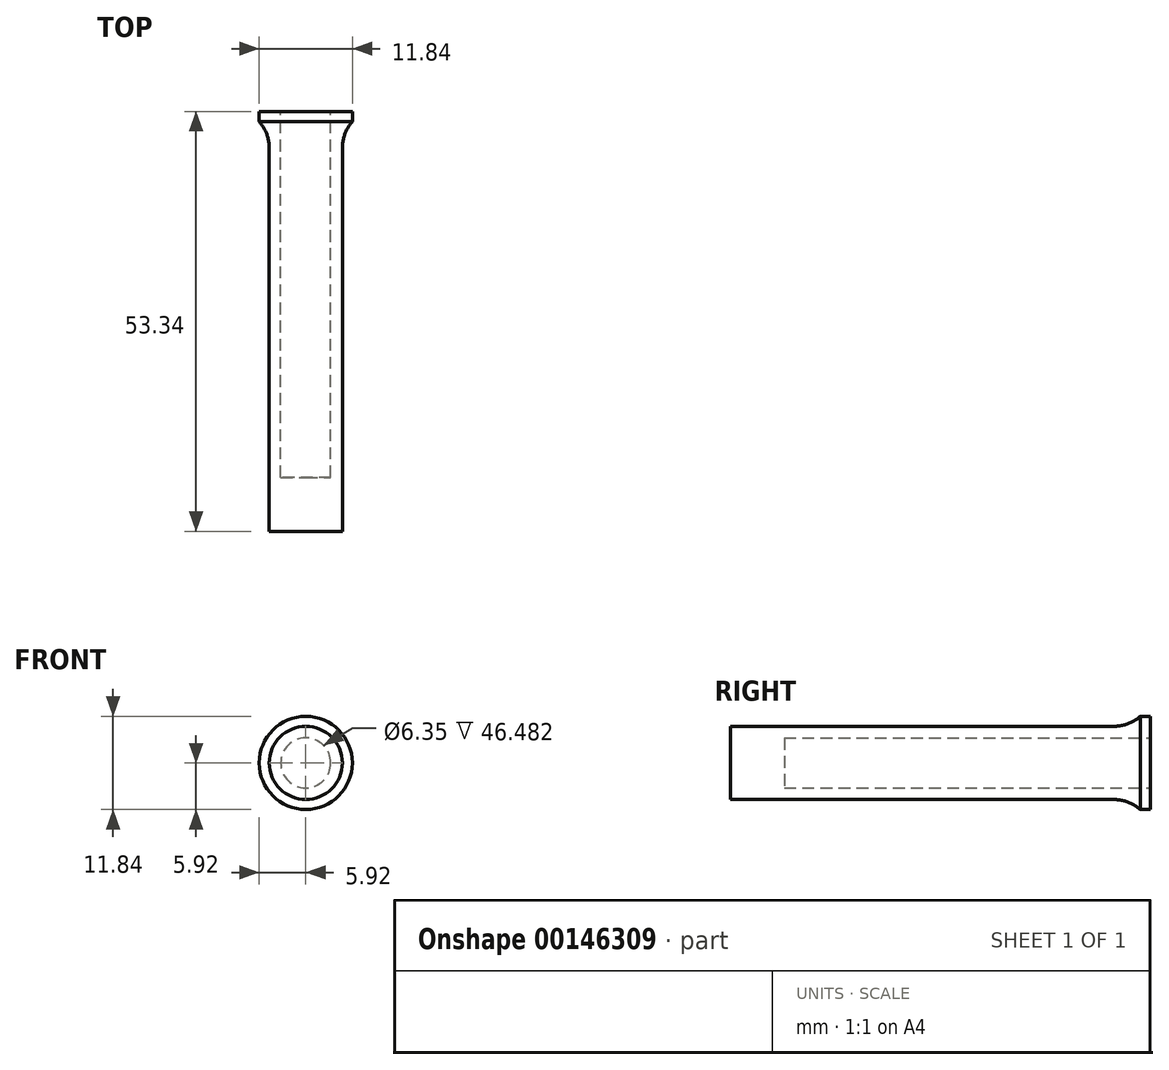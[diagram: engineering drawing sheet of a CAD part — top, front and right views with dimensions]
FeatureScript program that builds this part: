
annotation { "Feature Type Name" : "Feature", "Feature Type Description" : "" }
export const myFeature = defineFeature(function(context is Context, id is Id, definition is map)
    precondition{}
    {
        {
            var Q0;
            Q0=qCreatedBy(makeId("Top.planeOp"),FACE);
            var sketch = newSketch(context, id + "F0", { "sketchPlane" : qUnion([Q0])});
            skLineSegment(sketch, "E0", {"start": v(0, 0) * mm, "end": v(-4.65, 0) * mm});
            skLineSegment(sketch, "E1", {"start": v(-4.65, 0) * mm, "end": v(-4.65, 52.07) * mm});
            skLineSegment(sketch, "E2", {"start": v(-4.65, 53.34) * mm, "end": v(-3.18, 53.34) * mm});
            skLineSegment(sketch, "E3", {"start": v(-3.18, 53.34) * mm, "end": v(-3.17, 6.86) * mm});
            skLineSegment(sketch, "E4", {"start": v(-3.18, 6.86) * mm, "end": v(0, 6.86) * mm});
            skLineSegment(sketch, "E5", {"start": v(0, 6.86) * mm, "end": v(0, 0) * mm});
            skLineSegment(sketch, "E6", {"start": v(-4.65, 53.34) * mm, "end": v(-5.92, 53.34) * mm});
            skLineSegment(sketch, "E7", {"start": v(-5.92, 53.34) * mm, "end": v(-5.92, 52.07) * mm});
            skLineSegment(sketch, "E8", {"start": v(-5.92, 52.07) * mm, "end": v(-4.65, 52.07) * mm});
            skSolve(sketch);
        }
        {
            var Q0;
            Q0 = qSketchRegion(id + "F0", true);
            var Q1;
            Q1=sQuery(id+"F0.wireOp",EDGE,"E5");
            revolve(context, id + "F1", {"entities" : qUnion([Q0]), "axis" : qUnion([Q1]), "revolveType" : RevolveType.FULL});
        }
        {
            var Q0;
            Q0=makeQuery(id+"F1.opRevolve","SWEPT_EDGE",EDGE,{"disambiguationData":[OSD([sQuery(id+"F0.wireOp",EDGE,"E1"),sQuery(id+"F0.wireOp",EDGE,"E8")])]});
            fillet(context, id + "F2", {"entities" : qUnion([Q0]), "radius" : 5.08 * mm, "tangentPropagation" : true, "allowEdgeOverflow" : false});
        }
    });
